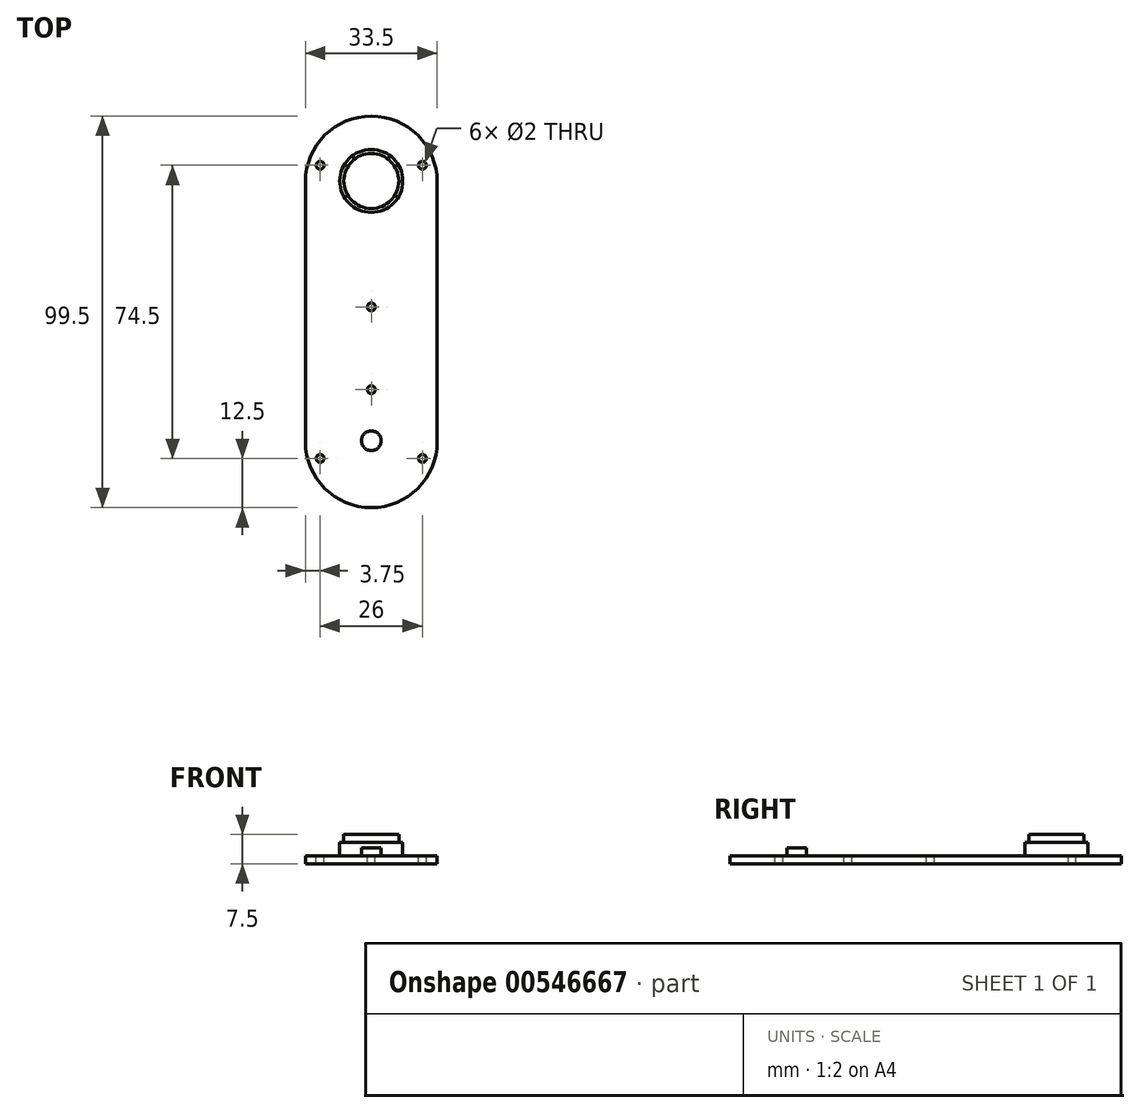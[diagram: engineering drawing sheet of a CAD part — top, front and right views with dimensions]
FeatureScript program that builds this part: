
annotation { "Feature Type Name" : "Feature", "Feature Type Description" : "" }
export const myFeature = defineFeature(function(context is Context, id is Id, definition is map)
    precondition{}
    {
        {
            var Q0;
            Q0=qCreatedBy(makeId("Top.planeOp"),FACE);
            var sketch = newSketch(context, id + "F0", { "sketchPlane" : qUnion([Q0])});
            skLineSegment(sketch, "E0", {"start": v(-96.93, -49.75) * mm, "end": v(93.91, -49.75) * mm, "construction": true});
            skLineSegment(sketch, "E1", {"start": v(-99.2, 49.75) * mm, "end": v(105.24, 49.75) * mm, "construction": true});
            skArc(sketch, "E2", {"start": v(16.75, 33) * mm, "mid": v(11.84, 44.84) * mm, "end": v(0, 49.75) * mm});
            skArc(sketch, "E3", {"start": v(0, -49.75) * mm, "mid": v(11.84, -44.84) * mm, "end": v(16.75, -33) * mm});
            skLineSegment(sketch, "E4.trimOffspring", {"start": v(16.75, 33) * mm, "end": v(16.75, -33) * mm});
            skArc(sketch, "E5.MirrorCS", {"start": v(-16.75, 33) * mm, "mid": v(-11.84, 44.84) * mm, "end": v(0, 49.75) * mm});
            skLineSegment(sketch, "E6.MirrorCS", {"start": v(-16.75, 33) * mm, "end": v(-16.75, -33) * mm});
            skArc(sketch, "E7.MirrorCS", {"start": v(0, -49.75) * mm, "mid": v(-11.84, -44.84) * mm, "end": v(-16.75, -33) * mm});
            skSolve(sketch);
        }
        {
            var Q0;
            Q0=qSketchRegion(id+"F0",true);
            extrude(context, id + "F1", {"entities" : qUnion([Q0]), "depth" : 2 * mm});
        }
        {
            var Q0;
            Q0=makeQuery(id+"F1.opExtrude","CAP_FACE",FACE,{"disambiguationData":[OSD([sQuery(id+"F0.wireOp",EDGE,"E2"),sQuery(id+"F0.wireOp",EDGE,"E3"),sQuery(id+"F0.wireOp",EDGE,"E4.trimOffspring"),sQuery(id+"F0.wireOp",EDGE,"E5.MirrorCS"),sQuery(id+"F0.wireOp",EDGE,"E6.MirrorCS"),sQuery(id+"F0.wireOp",EDGE,"E7.MirrorCS")])],"isStart":false});
            var sketch = newSketch(context, id + "F2", { "sketchPlane" : qUnion([Q0])});
            skLineSegment(sketch, "E8", {"start": v(-13, -67.26) * mm, "end": v(-13, 68.17) * mm, "construction": true});
            skLineSegment(sketch, "E9", {"start": v(13, -68.02) * mm, "end": v(13, 71.72) * mm, "construction": true});
            skLineSegment(sketch, "E10", {"start": v(-30.03, -49.75) * mm, "end": v(26.5, -49.75) * mm, "construction": true});
            skLineSegment(sketch, "E11", {"start": v(-29.95, -37.25) * mm, "end": v(27.55, -37.25) * mm, "construction": true});
            skLineSegment(sketch, "E12", {"start": v(-32.6, -19.75) * mm, "end": v(26.44, -19.75) * mm, "construction": true});
            skLineSegment(sketch, "E13", {"start": v(-30.61, 1.25) * mm, "end": v(28.66, 1.25) * mm, "construction": true});
            skCircle(sketch, "E14", {"center": v(-13, -37.25) * mm, "radius": 1 * mm});
            skCircle(sketch, "E15", {"center": v(13, -37.25) * mm, "radius": 1 * mm});
            skCircle(sketch, "E16", {"center": v(0, 1.25) * mm, "radius": 1 * mm});
            skCircle(sketch, "E17", {"center": v(0, -19.75) * mm, "radius": 1 * mm});
            skCircle(sketch, "E18.MirrorC", {"center": v(13, 37.25) * mm, "radius": 1 * mm});
            skCircle(sketch, "E19.MirrorC", {"center": v(-13, 37.25) * mm, "radius": 1 * mm});
            skSolve(sketch);
        }
        {
            var Q0;
            Q0=qSketchRegion(id+"F2",true);
            extrude(context, id + "F3", {"entities" : qUnion([Q0]), "operationType" : NewBodyOperationType.REMOVE, "endBound" : BoundingType.THROUGH_ALL, "oppositeDirection" : true, "depth" : 25 * mm});
        }
        {
            var Q0;
            Q0=makeQuery(id+"F1.opExtrude","CAP_FACE",FACE,{"disambiguationData":[OSD([sQuery(id+"F0.wireOp",EDGE,"E2"),sQuery(id+"F0.wireOp",EDGE,"E3"),sQuery(id+"F0.wireOp",EDGE,"E4.trimOffspring"),sQuery(id+"F0.wireOp",EDGE,"E5.MirrorCS"),sQuery(id+"F0.wireOp",EDGE,"E6.MirrorCS"),sQuery(id+"F0.wireOp",EDGE,"E7.MirrorCS")])],"isStart":false});
            var sketch = newSketch(context, id + "F4", { "sketchPlane" : qUnion([Q0])});
            skLineSegment(sketch, "E20", {"start": v(-44.3, 49.75) * mm, "end": v(38.5, 49.75) * mm, "construction": true});
            skCircle(sketch, "E21", {"center": v(0, 33.25) * mm, "radius": 8 * mm});
            skSolve(sketch);
        }
        {
            var Q0;
            Q0=qSketchRegion(id+"F4",true);
            extrude(context, id + "F5", {"entities" : qUnion([Q0]), "operationType" : NewBodyOperationType.ADD, "depth" : 3.5 * mm});
        }
        {
            var Q0;
            Q0=makeQuery(id+"F5.opExtrude","CAP_FACE",FACE,{"disambiguationData":[OSD([sQuery(id+"F4.wireOp",EDGE,"E21")])],"isStart":false});
            var sketch = newSketch(context, id + "F6", { "sketchPlane" : qUnion([Q0])});
            skCircle(sketch, "E22", {"center": v(0, 33.25) * mm, "radius": 7 * mm});
            skSolve(sketch);
        }
        {
            var Q0;
            Q0=qSketchRegion(id+"F6",true);
            extrude(context, id + "F7", {"entities" : qUnion([Q0]), "operationType" : NewBodyOperationType.ADD, "depth" : 2 * mm});
        }
        {
            var Q0;
            Q0=makeQuery(id+"F1.opExtrude","CAP_FACE",FACE,{"disambiguationData":[OSD([sQuery(id+"F0.wireOp",EDGE,"E2"),sQuery(id+"F0.wireOp",EDGE,"E3"),sQuery(id+"F0.wireOp",EDGE,"E4.trimOffspring"),sQuery(id+"F0.wireOp",EDGE,"E5.MirrorCS"),sQuery(id+"F0.wireOp",EDGE,"E6.MirrorCS"),sQuery(id+"F0.wireOp",EDGE,"E7.MirrorCS")])],"isStart":false});
            var sketch = newSketch(context, id + "F8", { "sketchPlane" : qUnion([Q0])});
            skLineSegment(sketch, "E23", {"start": v(-35.2, -49.75) * mm, "end": v(36.2, -49.75) * mm, "construction": true});
            skLineSegment(sketch, "E24", {"start": v(-34.12, -32.75) * mm, "end": v(36.82, -32.75) * mm, "construction": true});
            skCircle(sketch, "E25", {"center": v(0, -32.75) * mm, "radius": 2.5 * mm});
            skSolve(sketch);
        }
        {
            var Q0;
            Q0=qSketchRegion(id+"F8",true);
            extrude(context, id + "F9", {"entities" : qUnion([Q0]), "operationType" : NewBodyOperationType.ADD, "depth" : 2 * mm});
        }
    });
